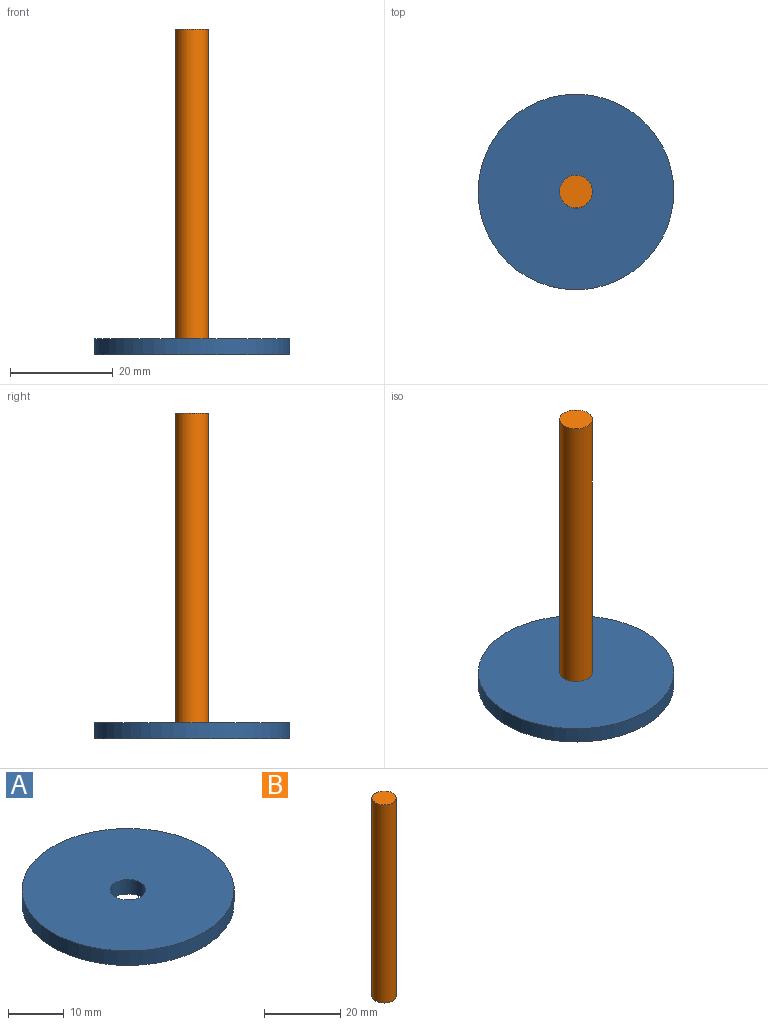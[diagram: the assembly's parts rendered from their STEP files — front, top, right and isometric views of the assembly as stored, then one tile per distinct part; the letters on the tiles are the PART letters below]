
ASSEMBLY  parts=2 mates=1
PART A: 4 faces, bbox 38.1x38.1x3.2 mm
  f0: cylinder r=3.17mm len=6.35mm, axis (0,0,-1), area 63.3mm2, adj f2,f3
  f1: cylinder r=19.05mm len=38.1mm, axis (0,0,-1), area 380mm2, adj f2,f3
  f2: plane 38.1x38.1mm, normal (0,0,1), area 1108.4mm2, adj f0,f1
  f3: plane 38.1x38.1mm, normal (0,0,-1), area 1108.4mm2, adj f0,f1
PART B: 3 faces, bbox 6.4x6.4x63.5 mm
  f0: plane 6.35x6.35mm, normal (0,0,1), area 31.7mm2, adj f1
  f1: cylinder r=3.17mm len=63.5mm, axis (0,0,-1), area 1266.8mm2, adj f0,f2
  f2: plane 6.35x6.35mm, normal (0,0,-1), area 31.7mm2, adj f1
PLACE A t=(-31.75,0,-69.85)mm
PLACE B t=(-31.75,0,-69.85)mm
MATE fastened A.f0 <-> B.f1  axis (0,0,-1) through (0,0,0)mm
